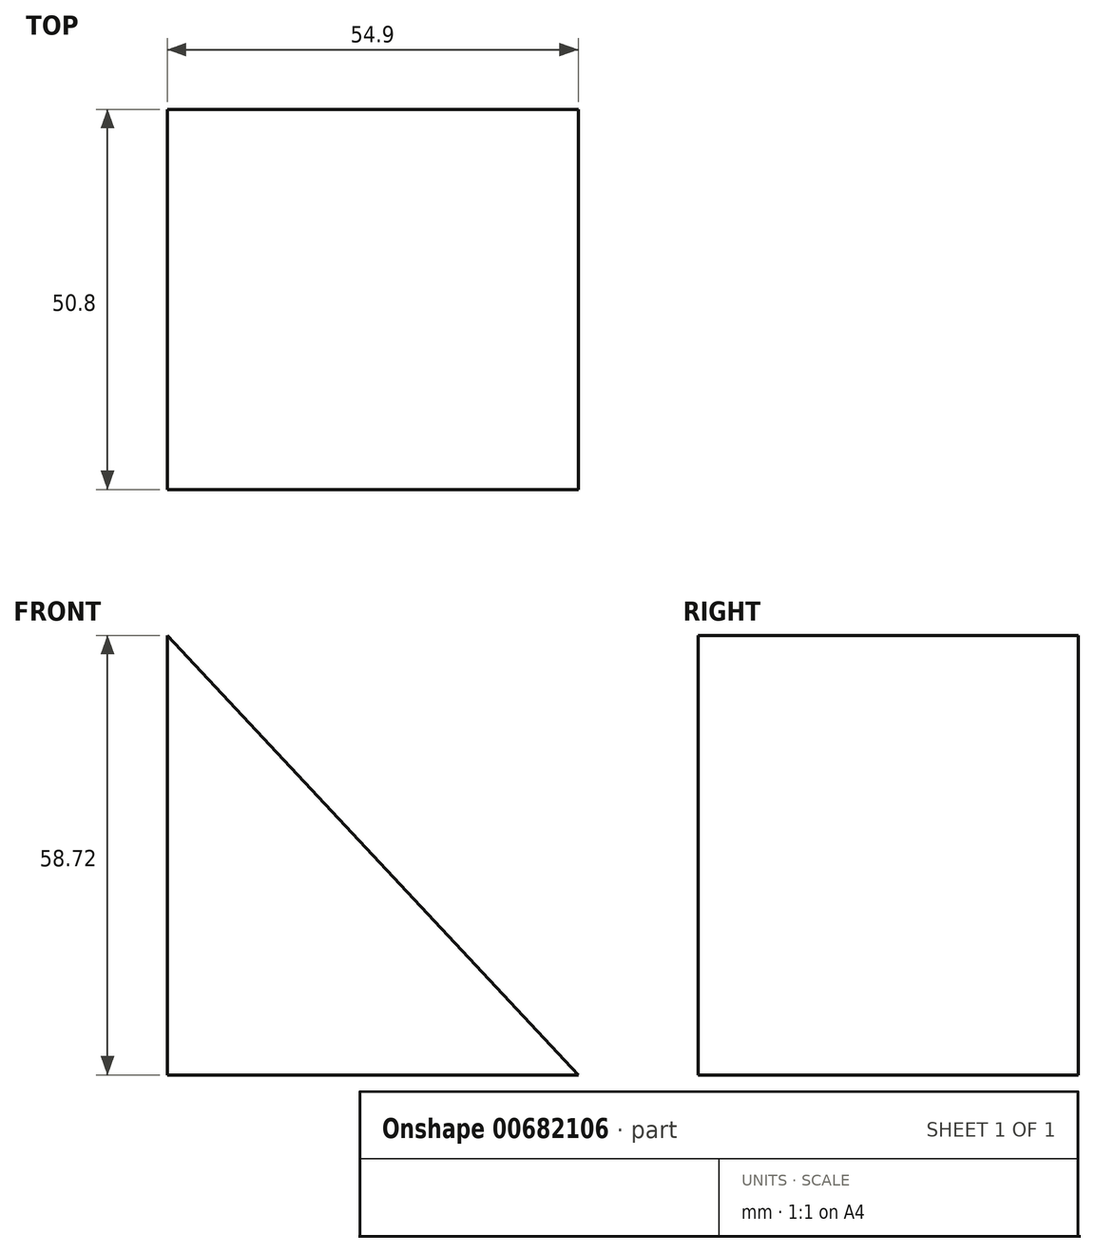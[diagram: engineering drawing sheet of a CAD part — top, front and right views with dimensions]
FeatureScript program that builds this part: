
annotation { "Feature Type Name" : "Feature", "Feature Type Description" : "" }
export const myFeature = defineFeature(function(context is Context, id is Id, definition is map)
    precondition{}
    {
        {
            var Q0;
            Q0=qCreatedBy(makeId("Front.planeOp"),FACE);
            var sketch = newSketch(context, id + "F0", { "sketchPlane" : qUnion([Q0])});
            skLineSegment(sketch, "E0", {"start": v(-54.9, 58.72) * mm, "end": v(-54.9, 0) * mm});
            skLineSegment(sketch, "E1", {"start": v(-54.9, 0) * mm, "end": v(0, 0) * mm});
            skLineSegment(sketch, "E2", {"start": v(0, 0) * mm, "end": v(-54.9, 58.72) * mm});
            skSolve(sketch);
        }
        {
            var Q0;
            Q0 = qSketchRegion(id + "F0", true);
            extrude(context, id + "F1", {"entities" : qUnion([Q0]), "depth" : 50.8 * mm, "offsetDistance" : 25.4 * mm});
        }
    });
